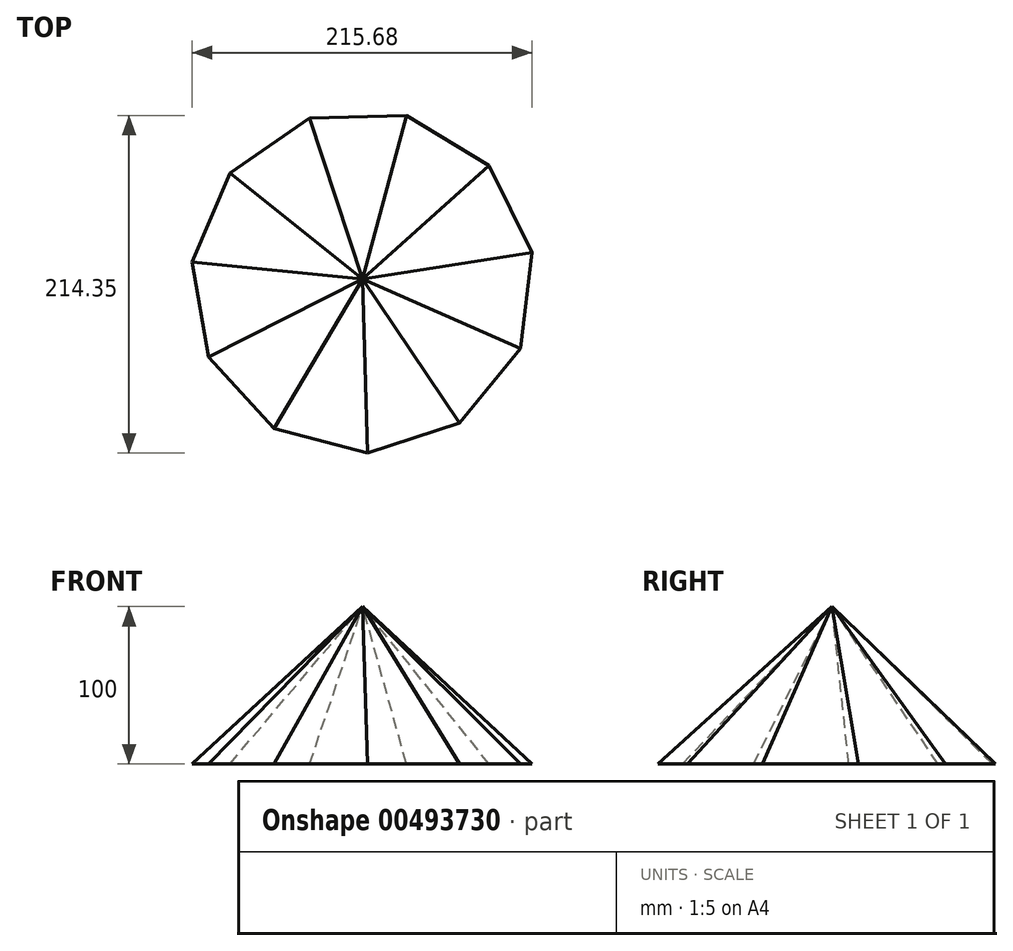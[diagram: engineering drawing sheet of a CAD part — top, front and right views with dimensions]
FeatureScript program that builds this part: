
annotation { "Feature Type Name" : "Feature", "Feature Type Description" : "" }
export const myFeature = defineFeature(function(context is Context, id is Id, definition is map)
    precondition{}
    {
        {
            var Q0;
            Q0=qCreatedBy(makeId("Top.planeOp"),FACE);
            var sketch = newSketch(context, id + "F0", { "sketchPlane" : qUnion([Q0])});
            skCircle(sketch, "E0.cCircle", {"center": v(0, 0) * mm, "radius": 109 * mm, "construction": true});
            skLineSegment(sketch, "E0.0", {"start": v(-97.83, -48.05) * mm, "end": v(-108.28, 12.46) * mm});
            skLineSegment(sketch, "E0.1", {"start": v(-108.28, 12.46) * mm, "end": v(-84.35, 69.03) * mm});
            skLineSegment(sketch, "E0.2", {"start": v(-84.35, 69.03) * mm, "end": v(-33.64, 103.67) * mm});
            skLineSegment(sketch, "E0.3", {"start": v(-33.64, 103.67) * mm, "end": v(27.75, 105.4) * mm});
            skLineSegment(sketch, "E0.4", {"start": v(27.75, 105.4) * mm, "end": v(80.33, 73.67) * mm});
            skLineSegment(sketch, "E0.5", {"start": v(80.33, 73.67) * mm, "end": v(107.4, 18.55) * mm});
            skLineSegment(sketch, "E0.6", {"start": v(107.4, 18.55) * mm, "end": v(100.38, -42.47) * mm});
            skLineSegment(sketch, "E0.7", {"start": v(100.38, -42.47) * mm, "end": v(61.49, -90) * mm});
            skLineSegment(sketch, "E0.8", {"start": v(61.49, -90) * mm, "end": v(3.07, -108.95) * mm});
            skLineSegment(sketch, "E0.9", {"start": v(3.07, -108.95) * mm, "end": v(-56.32, -93.31) * mm});
            skLineSegment(sketch, "E0.10", {"start": v(-56.32, -93.31) * mm, "end": v(-97.83, -48.05) * mm});
            skSolve(sketch);
        }
        {
            var Q0;
            Q0=qCreatedBy(makeId("Top.planeOp"),FACE);
            cPlane(context, id + "F1", {"entities" : qUnion([Q0]), "cplaneType" : CPlaneType.OFFSET, "offset" : 100 * mm, "width" : 150 * mm, "height" : 150 * mm});
        }
        {
            var Q0;
            Q0=qCreatedBy(id+"F1.planeOp",FACE);
            var sketch = newSketch(context, id + "F2", { "sketchPlane" : qUnion([Q0])});
            skPoint(sketch, "E1", {"position": v(0, 1.62) * mm});
            skSolve(sketch);
        }
        {
            var Q0;
            Q0=makeQuery(id+"F0.imprint","IMPRINT",FACE,{"disambiguationData":[TD([[makeQuery(id+"F0.imprint","IMPRINT",EDGE,{"derivedFrom":sQuery(id+"F0.wireOp",EDGE,"E0.0")}),-1.0]])]});
            var Q1;
            Q1=sQuery(id+"F2.wireOp",VERTEX,"E1");
            loft(context, id + "F3", {"sheetProfilesArray" : [{ "sheetProfileEntities" : qUnion([Q0]) }, { "sheetProfileEntities" : qUnion([Q1]) }]});
        }
    });
